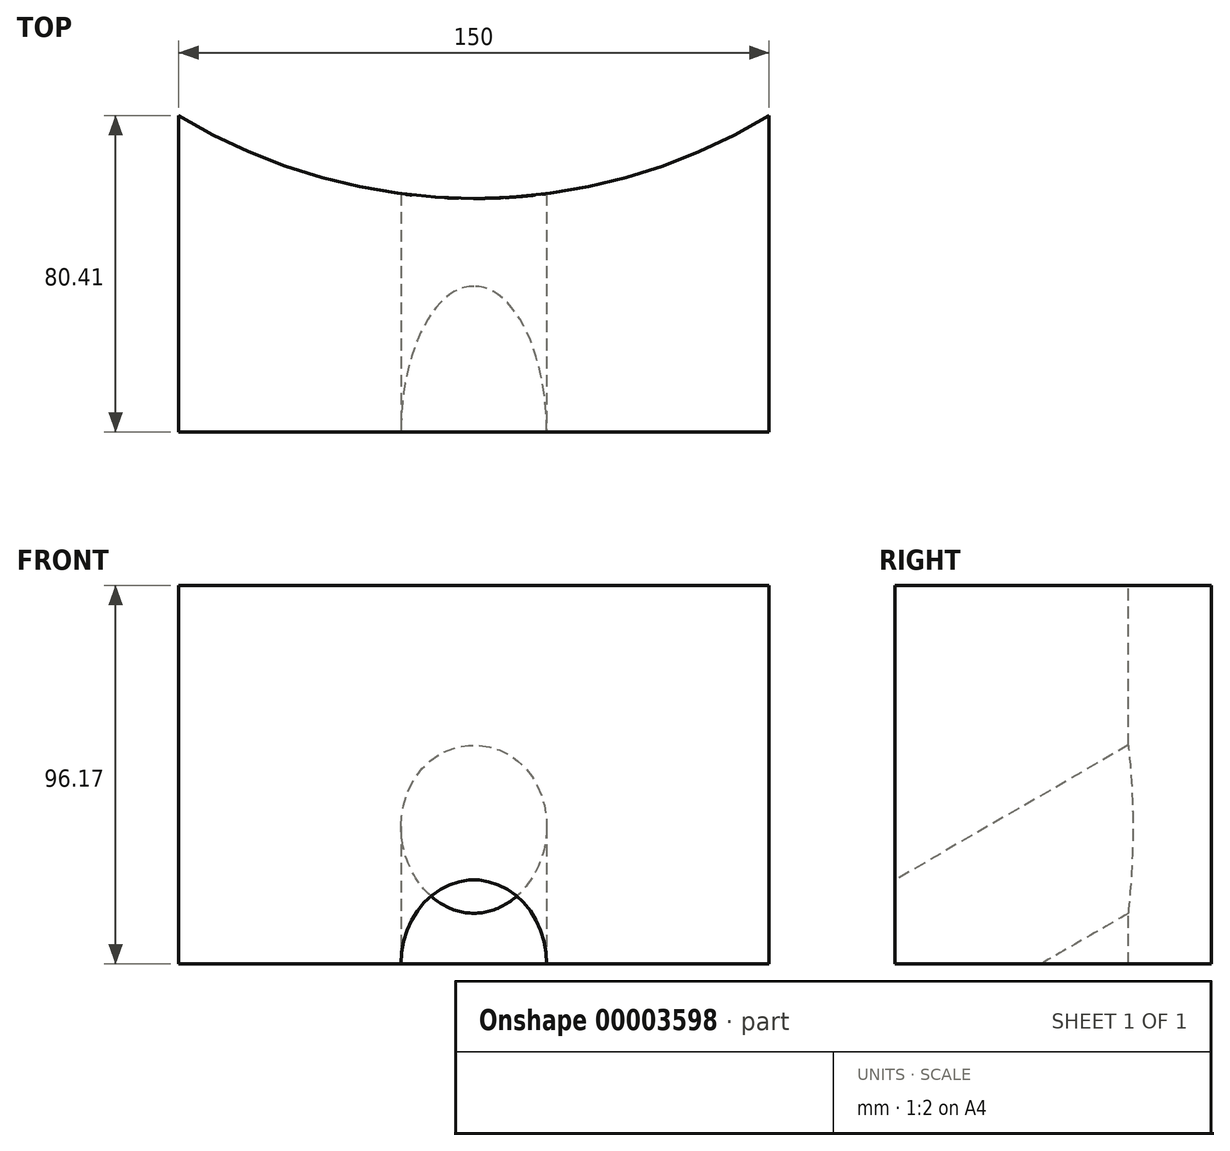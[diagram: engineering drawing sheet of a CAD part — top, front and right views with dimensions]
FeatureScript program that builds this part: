
annotation { "Feature Type Name" : "Feature", "Feature Type Description" : "" }
export const myFeature = defineFeature(function(context is Context, id is Id, definition is map)
    precondition{}
    {
        {
            var Q0;
            Q0=qCreatedBy(makeId("Top.planeOp"),FACE);
            var sketch = newSketch(context, id + "F0", { "sketchPlane" : qUnion([Q0])});
            skLineSegment(sketch, "E0.rect.bottom", {"start": v(-75, 100) * mm, "end": v(75, 100) * mm});
            skLineSegment(sketch, "E0.rect.top", {"start": v(-75, -100) * mm, "end": v(75, -100) * mm});
            skLineSegment(sketch, "E0.rect.left", {"start": v(-75, 100) * mm, "end": v(-75, -100) * mm});
            skLineSegment(sketch, "E0.rect.right", {"start": v(75, 100) * mm, "end": v(75, -100) * mm});
            skPoint(sketch, "E0.rect.middle", {"position": v(0, 0) * mm});
            skLineSegment(sketch, "E1", {"start": v(-113.15, -100) * mm, "end": v(150.44, -100) * mm, "construction": true});
            skSolve(sketch);
        }
        {
            var Q0;
            Q0 = qSketchRegion(id + "F0", true);
            extrude(context, id + "F1", {"entities" : qUnion([Q0]), "depth" : 200 * mm});
        }
        {
            var Q0;
            Q0=makeQuery(id+"F1.opExtrude","CAP_EDGE",EDGE,{"disambiguationData":[OSD([sQuery(id+"F0.wireOp",EDGE,"E0.rect.top")])],"isStart":true});
            cPlane(context, id + "F2", {"entities" : qUnion([Q0]), "cplaneType" : CPlaneType.LINE_ANGLE, "offset" : 150 * mm, "angle" : 120 * degree, "width" : 150 * mm, "height" : 150 * mm});
        }
        {
            var Q0;
            Q0=qCreatedBy(id+"F2.planeOp",FACE);
            var sketch = newSketch(context, id + "F3", { "sketchPlane" : qUnion([Q0])});
            skLineSegment(sketch, "E2", {"start": v(0, -86.6) * mm, "end": v(0, -161.33) * mm, "construction": true});
            skSolve(sketch);
        }
        {
            var Q0;
            Q0=sQuery(id+"F3.wireOp",EDGE,"E2");
            var Q1;
            Q1=sQuery(id+"F3.wireOp",VERTEX,"E2.start");
            cPlane(context, id + "F4", {"entities" : qUnion([Q0, Q1]), "cplaneType" : CPlaneType.LINE_POINT, "offset" : 150 * mm, "width" : 150 * mm, "height" : 150 * mm});
        }
        {
            var Q0;
            Q0=qCreatedBy(id+"F4.planeOp",FACE);
            var sketch = newSketch(context, id + "F5", { "sketchPlane" : qUnion([Q0])});
            skCircle(sketch, "E3", {"center": v(0, 50) * mm, "radius": 18.5 * mm});
            skSolve(sketch);
        }
        {
            var Q0;
            Q0=makeQuery(id+"F5.imprint","IMPRINT",FACE,{"disambiguationData":[TD([[makeQuery(id+"F5.imprint","IMPRINT",EDGE,{"derivedFrom":sQuery(id+"F5.wireOp",EDGE,"E3")}),1.0]])]});
            extrude(context, id + "F6", {"entities" : qUnion([Q0]), "operationType" : NewBodyOperationType.REMOVE, "endBound" : BoundingType.THROUGH_ALL, "oppositeDirection" : true, "depth" : 248.56 * mm});
        }
        {
            var Q0;
            Q0=makeQuery(id+"F1.opExtrude","CAP_FACE",FACE,{"disambiguationData":[OSD([sQuery(id+"F0.wireOp",EDGE,"E0.rect.bottom"),sQuery(id+"F0.wireOp",EDGE,"E0.rect.top"),sQuery(id+"F0.wireOp",EDGE,"E0.rect.left"),sQuery(id+"F0.wireOp",EDGE,"E0.rect.right")])],"isStart":false});
            cPlane(context, id + "F7", {"entities" : qUnion([Q0]), "cplaneType" : CPlaneType.OFFSET, "offset" : 0 * mm, "width" : 150 * mm, "height" : 150 * mm});
        }
        {
            var Q0;
            Q0=qCreatedBy(id+"F7.planeOp",FACE);
            var sketch = newSketch(context, id + "F8", { "sketchPlane" : qUnion([Q0])});
            skCircle(sketch, "E4", {"center": v(0, 103.34) * mm, "radius": 144 * mm});
            skLineSegment(sketch, "E5", {"start": v(0, -100.66) * mm, "end": v(0, -40.66) * mm, "construction": true});
            skSolve(sketch);
        }
        {
            var Q0;
            Q0=makeQuery(id+"F8.imprint","IMPRINT",FACE,{"disambiguationData":[TD([[makeQuery(id+"F8.imprint","IMPRINT",EDGE,{"derivedFrom":sQuery(id+"F8.wireOp",EDGE,"E4")}),1.0]])]});
            var Q1;
            Q1=sQuery(id+"F8.wireOp",EDGE,"E4");
            extrude(context, id + "F9", {"entities" : qUnion([Q0]), "operationType" : NewBodyOperationType.REMOVE, "surfaceEntities" : qUnion([Q1]), "endBound" : BoundingType.THROUGH_ALL, "oppositeDirection" : true, "depth" : 25 * mm});
        }
        {
            var Q0;
            Q0=makeQuery(id+"F1.opExtrude","SWEPT_FACE",FACE,{"disambiguationData":[OSD([sQuery(id+"F0.wireOp",EDGE,"E0.rect.right")])]});
            cPlane(context, id + "F10", {"entities" : qUnion([Q0]), "cplaneType" : CPlaneType.OFFSET, "offset" : 0 * mm, "width" : 150 * mm, "height" : 150 * mm});
        }
        {
            var Q0;
            Q0=qCreatedBy(id+"F10.planeOp",FACE);
            var sketch = newSketch(context, id + "F11", { "sketchPlane" : qUnion([Q0])});
            skLineSegment(sketch, "E6.bottom", {"start": v(3.95, 216.17) * mm, "end": v(-105.05, 216.17) * mm});
            skLineSegment(sketch, "E6.top", {"start": v(3.95, 96.17) * mm, "end": v(-105.05, 96.17) * mm});
            skLineSegment(sketch, "E6.left", {"start": v(3.95, 216.17) * mm, "end": v(3.95, 96.17) * mm});
            skLineSegment(sketch, "E6.right", {"start": v(-105.05, 216.17) * mm, "end": v(-105.05, 96.17) * mm});
            skSolve(sketch);
        }
        {
            var Q0;
            Q0 = qSketchRegion(id + "F11", true);
            extrude(context, id + "F12", {"entities" : qUnion([Q0]), "operationType" : NewBodyOperationType.REMOVE, "endBound" : BoundingType.THROUGH_ALL, "oppositeDirection" : true, "depth" : 25 * mm});
        }
    });
